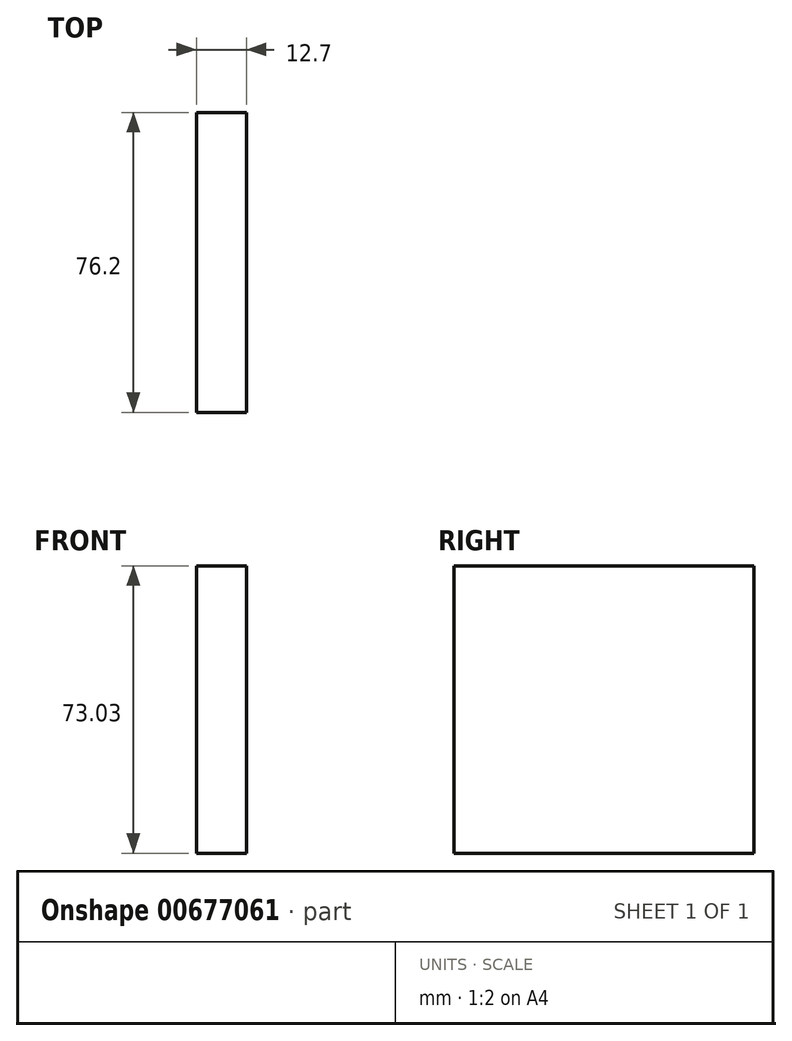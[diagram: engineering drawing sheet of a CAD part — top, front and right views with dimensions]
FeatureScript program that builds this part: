
annotation { "Feature Type Name" : "Feature", "Feature Type Description" : "" }
export const myFeature = defineFeature(function(context is Context, id is Id, definition is map)
    precondition{}
    {
        {
            var Q0;
            Q0=qCreatedBy(makeId("Right.planeOp"),FACE);
            var sketch = newSketch(context, id + "F0", { "sketchPlane" : qUnion([Q0])});
            skLineSegment(sketch, "E0.bottom", {"start": v(-42.04, -62.32) * mm, "end": v(34.16, -62.32) * mm});
            skLineSegment(sketch, "E0.top", {"start": v(-42.04, 10.7) * mm, "end": v(34.16, 10.7) * mm});
            skLineSegment(sketch, "E0.left", {"start": v(-42.04, -62.32) * mm, "end": v(-42.04, 10.7) * mm});
            skLineSegment(sketch, "E0.right", {"start": v(34.16, -62.32) * mm, "end": v(34.16, 10.7) * mm});
            skSolve(sketch);
        }
        {
            var Q0;
            Q0=makeQuery(id+"F0.imprint","IMPRINT",FACE,{"disambiguationData":[TD([[makeQuery(id+"F0.imprint","IMPRINT",EDGE,{"derivedFrom":sQuery(id+"F0.wireOp",EDGE,"E0.bottom")}),1.0]])]});
            extrude(context, id + "F1", {"entities" : qUnion([Q0]), "oppositeDirection" : true, "depth" : 12.7 * mm, "offsetDistance" : 25.4 * mm});
        }
    });
